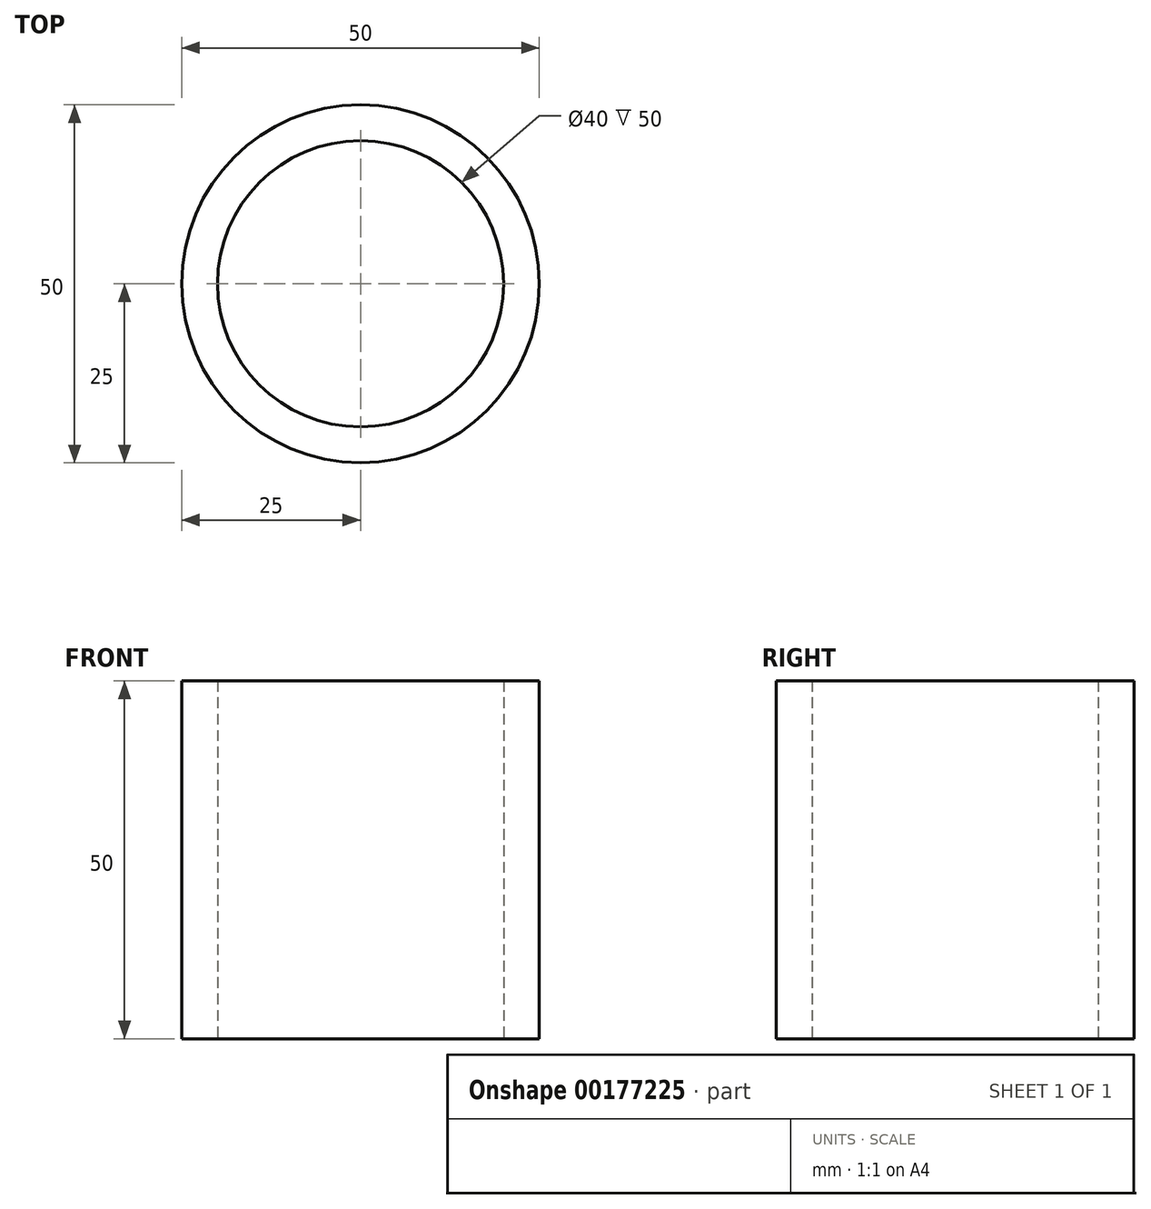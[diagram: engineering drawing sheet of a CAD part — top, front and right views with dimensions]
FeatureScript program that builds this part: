
annotation { "Feature Type Name" : "Feature", "Feature Type Description" : "" }
export const myFeature = defineFeature(function(context is Context, id is Id, definition is map)
    precondition{}
    {
        {
            var Q0;
            Q0=qCreatedBy(makeId("Top.planeOp"),FACE);
            var sketch = newSketch(context, id + "F0", { "sketchPlane" : qUnion([Q0])});
            skCircle(sketch, "E0", {"center": v(0, 0) * mm, "radius": 25 * mm});
            skCircle(sketch, "E1", {"center": v(0, 0) * mm, "radius": 20 * mm});
            skSolve(sketch);
        }
        {
            var Q0;
            Q0=makeQuery(id+"F0.imprint","IMPRINT",FACE,{"disambiguationData":[TD([[makeQuery(id+"F0.imprint","IMPRINT",EDGE,{"derivedFrom":sQuery(id+"F0.wireOp",EDGE,"E0")}),1.0]])]});
            extrude(context, id + "F1", {"entities" : qUnion([Q0]), "depth" : 50 * mm});
        }
    });
